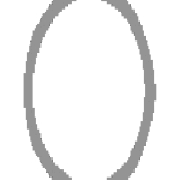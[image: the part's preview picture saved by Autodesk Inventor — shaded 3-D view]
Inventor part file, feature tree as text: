
AUTODESK INVENTOR PART (.ipt)
format: ipt  version: 2021 (Build 250183000, 183)  size: 127,488 bytes
history: native  units: in
note: dims shown in document units (in); Inventor stores cm internally (conversion verified against a paired STEP export)
features: other x4, plane x4, sketch x4, extrude x1, boolean_combine x1
ambient origin geometry x8: Origin, YZ Plane, XZ Plane, XY Plane, X Axis, Y Axis, Z Axis, Center Point
bodies: Solid1 (feature_tree), Body (feature_tree), Solid2 (feature_tree)
feature tree (14):
  other  "Driven Length"
  other  "Frame Generator"
  other  "Start Plane"
  other  "End Plane"
  plane  "Work Plane4"
  plane  "Work Plane5"
  plane  "Work Plane6"
  extrude  "Extrusion3"  Depth=0.065in
  boolean_combine  "Combine1"
  sketch  "Sketch"  dims[d5=11.5in d6=0.12in d7=0.0in d8=90.0deg d9=11.5in d10=0.12in d11=0.0in]
  sketch  "Sketch2"  dims[d0=1.0in d1=0.065in]
  plane  "Work Plane3"
  sketch  "Sketch3"  dims[d2=11.5in]
  sketch  "Sketch4"  dims[d4=-0.0in]
